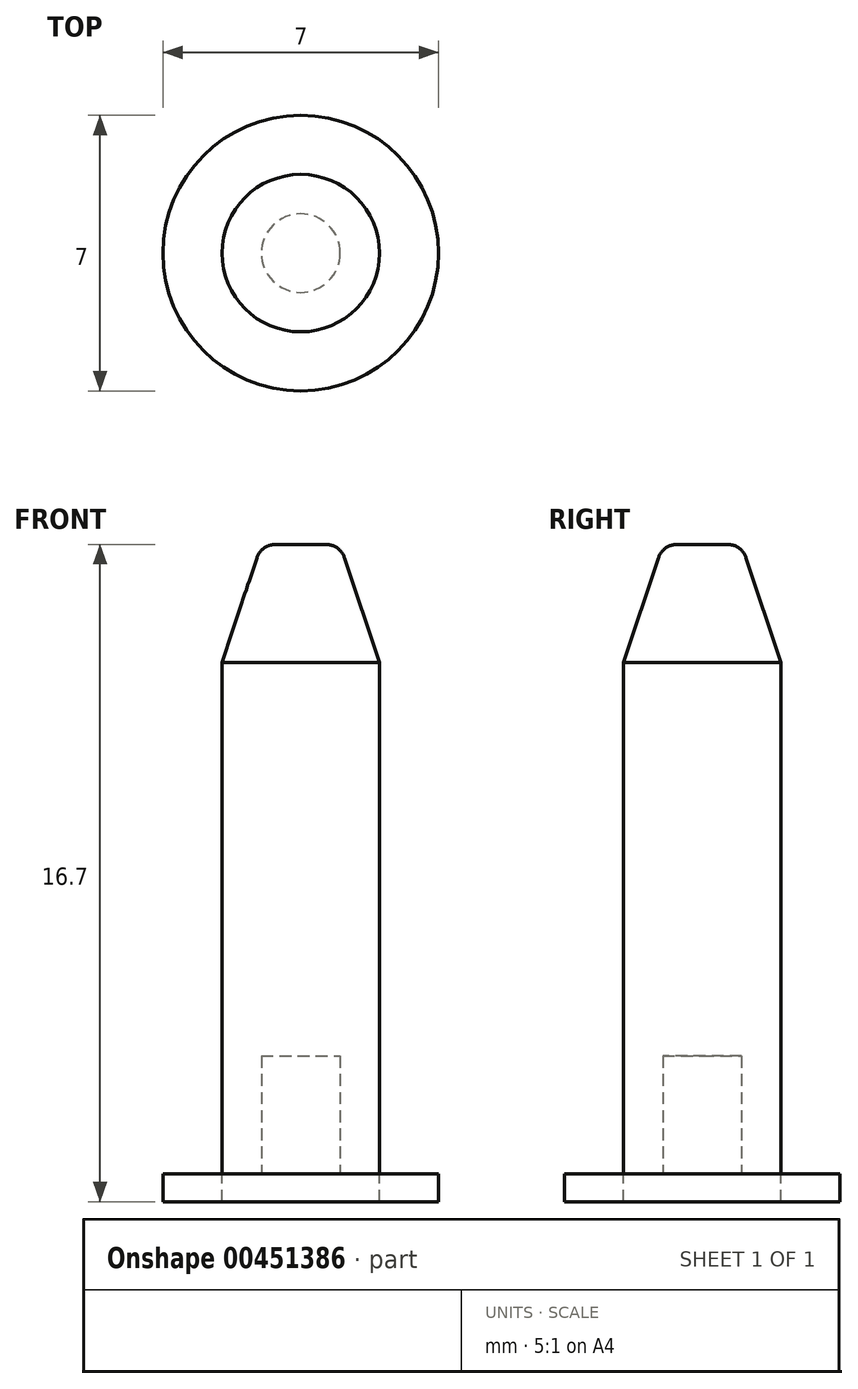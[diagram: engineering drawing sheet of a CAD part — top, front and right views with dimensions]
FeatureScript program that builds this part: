
annotation { "Feature Type Name" : "Feature", "Feature Type Description" : "" }
export const myFeature = defineFeature(function(context is Context, id is Id, definition is map)
    precondition{}
    {
        {
            var Q0;
            Q0=qCreatedBy(makeId("Front.planeOp"),FACE);
            var sketch = newSketch(context, id + "F0", { "sketchPlane" : qUnion([Q0])});
            skLineSegment(sketch, "E0", {"start": v(0, 0) * mm, "end": v(0, 16) * mm});
            skLineSegment(sketch, "E1", {"start": v(0, 16) * mm, "end": v(1, 16) * mm});
            skLineSegment(sketch, "E2", {"start": v(1, 16) * mm, "end": v(2, 13) * mm});
            skLineSegment(sketch, "E3", {"start": v(2, 13) * mm, "end": v(2, 0) * mm});
            skLineSegment(sketch, "E4", {"start": v(2, 0) * mm, "end": v(0, 0) * mm});
            skLineSegment(sketch, "E5", {"start": v(1, 0) * mm, "end": v(1, 3) * mm});
            skLineSegment(sketch, "E6", {"start": v(1, 3) * mm, "end": v(0, 3) * mm});
            skSolve(sketch);
        }
        {
            var Q0;
            {var subQ1=sQuery(id+"F0.wireOp",EDGE,"E1");Q0=makeQuery(id+"F0.imprint","IMPRINT",FACE,{"disambiguationData":[TD([[makeQuery(id+"F0.imprint","IMPRINT",EDGE,{"derivedFrom":subQ1}),-1.0]])]});}
            var Q1;
            Q1=sQuery(id+"F0.wireOp",EDGE,"E0");
            revolve(context, id + "F1", {"entities" : qUnion([Q0]), "axis" : qUnion([Q1]), "revolveType" : RevolveType.FULL});
        }
        {
            var Q0;
            Q0=makeQuery(id+"F1.opRevolve","SWEPT_FACE",FACE,{"disambiguationData":[OSD([sQuery(id+"F0.wireOp",EDGE,"E4")])]});
            var sketch = newSketch(context, id + "F2", { "sketchPlane" : qUnion([Q0])});
            skCircle(sketch, "E7", {"center": v(0, 0) * mm, "radius": 3.5 * mm});
            skCircle(sketch, "E8", {"center": v(0, 0) * mm, "radius": 1.6 * mm});
            skSolve(sketch);
        }
        {
            var Q0;
            Q0=makeQuery(id+"F2.imprint","IMPRINT",FACE,{"disambiguationData":[TD([[makeQuery(id+"F2.imprint","IMPRINT",EDGE,{"derivedFrom":sQuery(id+"F2.wireOp",EDGE,"E7")}),1.0]])]});
            extrude(context, id + "F3", {"entities" : qUnion([Q0]), "depth" : 0.7 * mm});
        }
        {
            var Q0;
            Q0=makeQuery(id+"F1.opRevolve","SWEPT_EDGE",EDGE,{"disambiguationData":[OSD([sQuery(id+"F0.wireOp",EDGE,"E1"),sQuery(id+"F0.wireOp",EDGE,"E2")])]});
            fillet(context, id + "F4", {"entities" : qUnion([Q0]), "radius" : 0.5 * mm, "tangentPropagation" : true, "allowEdgeOverflow" : false});
        }
    });
